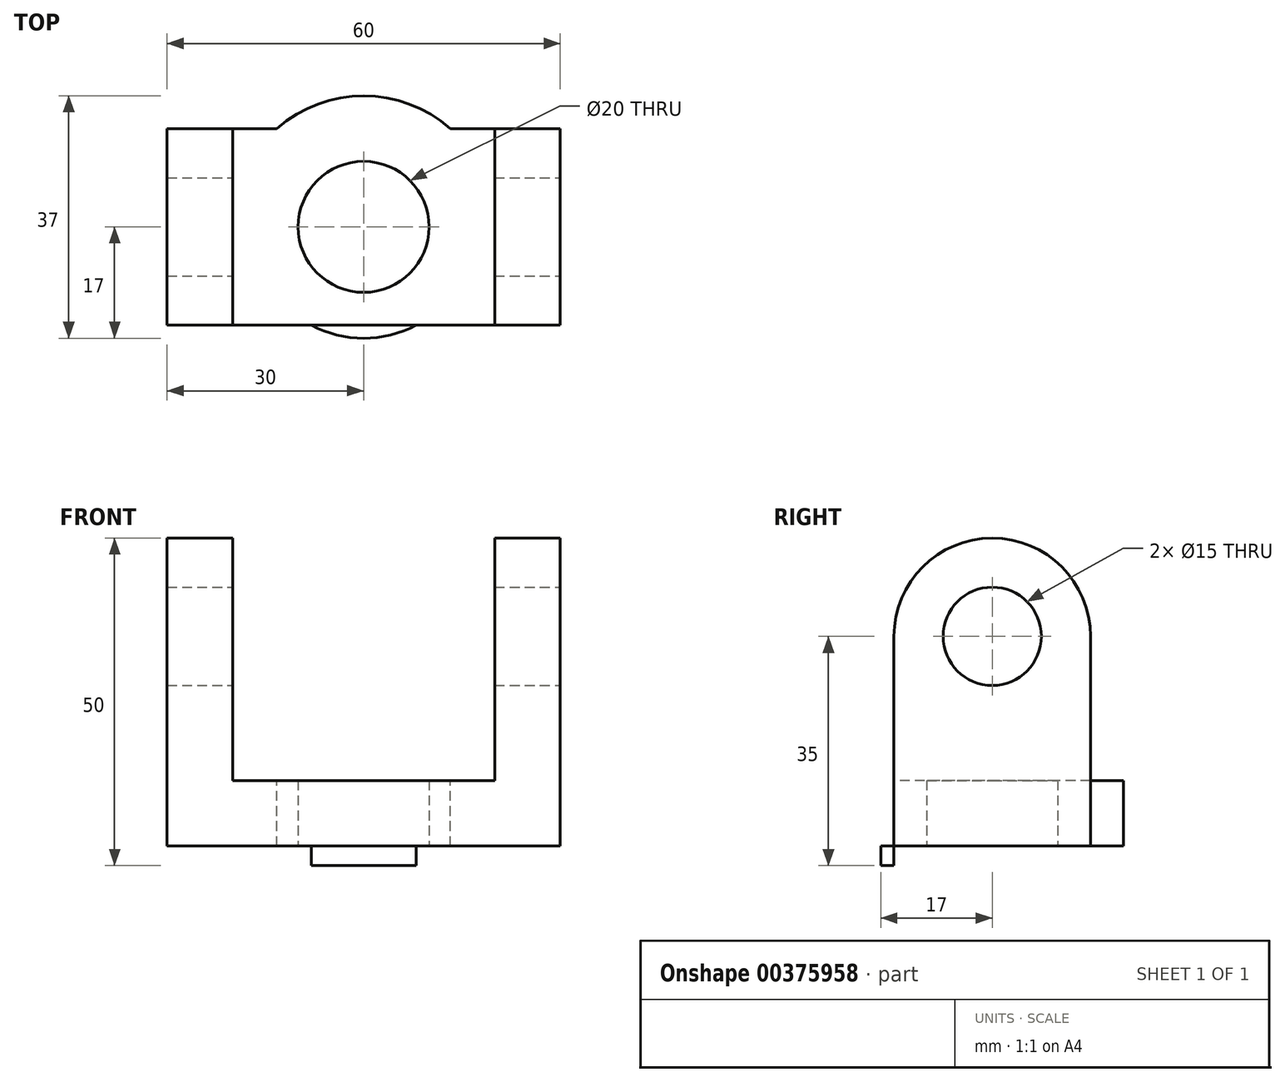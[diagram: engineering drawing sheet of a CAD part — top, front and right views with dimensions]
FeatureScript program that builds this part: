
annotation { "Feature Type Name" : "Feature", "Feature Type Description" : "" }
export const myFeature = defineFeature(function(context is Context, id is Id, definition is map)
    precondition{}
    {
        {
            var Q0;
            Q0=qCreatedBy(makeId("Top.planeOp"),FACE);
            var sketch = newSketch(context, id + "F0", { "sketchPlane" : qUnion([Q0])});
            skLineSegment(sketch, "E0.bottom", {"start": v(0, 0) * mm, "end": v(60, 0) * mm});
            skLineSegment(sketch, "E0.top", {"start": v(0, 30) * mm, "end": v(60, 30) * mm});
            skLineSegment(sketch, "E0.left", {"start": v(0, 0) * mm, "end": v(0, 30) * mm});
            skLineSegment(sketch, "E0.right", {"start": v(60, 0) * mm, "end": v(60, 30) * mm});
            skCircle(sketch, "E1", {"center": v(30, 15) * mm, "radius": 10 * mm});
            skPoint(sketch, "E1.centerSnap0", {"position": v(30, 30) * mm});
            skPoint(sketch, "E1.centerSnap1", {"position": v(0, 15) * mm});
            skSolve(sketch);
        }
        {
            var Q0;
            Q0 = qSketchRegion(id + "F0", true);
            extrude(context, id + "F1", {"entities" : qUnion([Q0]), "depth" : 10 * mm});
        }
        {
            var Q0;
            Q0=makeQuery(id+"F1.opExtrude","CAP_FACE",FACE,{"disambiguationData":[OSD([sQuery(id+"F0.wireOp",EDGE,"E0.bottom"),sQuery(id+"F0.wireOp",EDGE,"E0.top"),sQuery(id+"F0.wireOp",EDGE,"E0.left"),sQuery(id+"F0.wireOp",EDGE,"E0.right"),sQuery(id+"F0.wireOp",EDGE,"E1")])],"isStart":false});
            var sketch = newSketch(context, id + "F2", { "sketchPlane" : qUnion([Q0])});
            skArc(sketch, "E2", {"start": v(50, 15) * mm, "mid": v(30, 35) * mm, "end": v(10, 15) * mm});
            skPoint(sketch, "E3", {"position": v(0, 15) * mm});
            skPoint(sketch, "E4", {"position": v(60, 15) * mm});
            skLineSegment(sketch, "E5", {"start": v(0, 15) * mm, "end": v(60, 15) * mm, "construction": true});
            skArc(sketch, "E6.MirrorCS", {"start": v(50, 15) * mm, "mid": v(30, -5) * mm, "end": v(10, 15) * mm});
            skSolve(sketch);
        }
        {
            var Q0;
            {var subQ0=sQuery(id+"F2.wireOp",EDGE,"E2");var subQ1=makeQuery(id+"F1.opExtrude","CAP_EDGE",EDGE,{"disambiguationData":[OSD([sQuery(id+"F0.wireOp",EDGE,"E0.top")])],"isStart":false});var subQ2=makeQuery(id+"F2.imprint","INTERSECT",VERTEX,{"disambiguationData":[OD(0.0)],"derivedFrom":[subQ1,subQ0]});Q0=makeQuery(id+"F2.imprint","IMPRINT",FACE,{"disambiguationData":[TD([[makeQuery(id+"F2.imprint","IMPRINT",EDGE,{"disambiguationData":[TD([[subQ2,-1.0]])],"derivedFrom":subQ0}),1.0]])]});}
            var Q1;
            {var subQ0=sQuery(id+"F2.wireOp",EDGE,"E6.MirrorCS");var subQ1=makeQuery(id+"F1.opExtrude","CAP_EDGE",EDGE,{"disambiguationData":[OSD([sQuery(id+"F0.wireOp",EDGE,"E0.bottom")])],"isStart":false});var subQ2=makeQuery(id+"F2.imprint","INTERSECT",VERTEX,{"disambiguationData":[OD(0.0)],"derivedFrom":[subQ1,subQ0]});Q1=makeQuery(id+"F2.imprint","IMPRINT",FACE,{"disambiguationData":[TD([[makeQuery(id+"F2.imprint","IMPRINT",EDGE,{"disambiguationData":[TD([[subQ2,-1.0]])],"derivedFrom":subQ0}),-1.0]])]});}
            extrude(context, id + "F3", {"entities" : qUnion([Q0, Q1]), "operationType" : NewBodyOperationType.ADD, "oppositeDirection" : true, "depth" : 10 * mm});
        }
        {
            var Q0;
            {var subQ0=sQuery(id+"F0.wireOp",EDGE,"E0.bottom");var subQ1=sQuery(id+"F0.wireOp",EDGE,"E0.top");Q0=makeQuery(id+"F3.boolean.opBoolean","MERGE",FACE,{"derivedFrom":[makeQuery(id+"F1.opExtrude","CAP_FACE",FACE,{"disambiguationData":[OSD([subQ0,subQ1,sQuery(id+"F0.wireOp",EDGE,"E0.left"),sQuery(id+"F0.wireOp",EDGE,"E0.right"),sQuery(id+"F0.wireOp",EDGE,"E1")])],"isStart":true}),makeQuery(id+"F3.opExtrude","CAP_FACE",FACE,{"disambiguationData":[OSD([subQ1,sQuery(id+"F2.wireOp",EDGE,"E2")])],"isStart":false}),makeQuery(id+"F3.opExtrude","CAP_FACE",FACE,{"disambiguationData":[OSD([subQ0,sQuery(id+"F2.wireOp",EDGE,"E6.MirrorCS")])],"isStart":false})]});}
            var sketch = newSketch(context, id + "F4", { "sketchPlane" : qUnion([Q0])});
            skCircle(sketch, "E7", {"center": v(30, -15) * mm, "radius": 17 * mm});
            skSolve(sketch);
        }
        {
            var Q0;
            Q0=makeQuery(id+"F4.imprint","IMPRINT",FACE,{"disambiguationData":[TD([[makeQuery(id+"F4.imprint","IMPRINT",EDGE,{"derivedFrom":sQuery(id+"F4.wireOp",EDGE,"E7")}),1.0]])]});
            extrude(context, id + "F5", {"entities" : qUnion([Q0]), "operationType" : NewBodyOperationType.ADD, "depth" : 3 * mm});
        }
        {
            var Q0;
            Q0=makeQuery(id+"F1.opExtrude","SWEPT_FACE",FACE,{"disambiguationData":[OSD([sQuery(id+"F0.wireOp",EDGE,"E0.right")])]});
            var sketch = newSketch(context, id + "F6", { "sketchPlane" : qUnion([Q0])});
            skPoint(sketch, "E8.0", {"position": v(0, 10) * mm});
            skPoint(sketch, "E9.0", {"position": v(30, 10) * mm});
            skLineSegment(sketch, "E10.bottom", {"start": v(0, 10) * mm, "end": v(30, 10) * mm});
            skLineSegment(sketch, "E10.top", {"start": v(0, 32) * mm, "end": v(7.5, 32) * mm});
            skLineSegment(sketch, "E10.left", {"start": v(0, 10) * mm, "end": v(0, 32) * mm});
            skLineSegment(sketch, "E10.right", {"start": v(30, 10) * mm, "end": v(30, 32) * mm});
            skArc(sketch, "E11", {"start": v(30, 32) * mm, "mid": v(15, 47) * mm, "end": v(0, 32) * mm});
            skCircle(sketch, "E12", {"center": v(15, 32) * mm, "radius": 7.5 * mm});
            skLineSegment(sketch, "E13.trimOffspring", {"start": v(22.5, 32) * mm, "end": v(30, 32) * mm});
            skSolve(sketch);
        }
        {
            var Q0;
            Q0 = qSketchRegion(id + "F6", true);
            var Q1;
            Q1=makeQuery(id+"F1.opExtrude","SWEPT_FACE",FACE,{"disambiguationData":[OSD([sQuery(id+"F0.wireOp",EDGE,"E0.left")])]});
            extrude(context, id + "F7", {"entities" : qUnion([Q0]), "operationType" : NewBodyOperationType.ADD, "endBound" : BoundingType.UP_TO_SURFACE, "oppositeDirection" : true, "endBoundEntityFace" : qUnion([Q1]), "depth" : 25 * mm});
        }
        {
            var Q0;
            Q0=qCreatedBy(makeId("Front.planeOp"),FACE);
            var sketch = newSketch(context, id + "F8", { "sketchPlane" : qUnion([Q0])});
            skPoint(sketch, "E14.0", {"position": v(30, 10) * mm});
            skLineSegment(sketch, "E15.bottom", {"start": v(10, 51) * mm, "end": v(50, 51) * mm});
            skLineSegment(sketch, "E15.top", {"start": v(10, 10) * mm, "end": v(50, 10) * mm});
            skLineSegment(sketch, "E15.left", {"start": v(10, 51) * mm, "end": v(10, 10) * mm});
            skLineSegment(sketch, "E15.right", {"start": v(50, 51) * mm, "end": v(50, 10) * mm});
            skSolve(sketch);
        }
        {
            var Q0;
            Q0 = qSketchRegion(id + "F8", true);
            extrude(context, id + "F9", {"entities" : qUnion([Q0]), "operationType" : NewBodyOperationType.REMOVE, "endBound" : BoundingType.THROUGH_ALL, "oppositeDirection" : true, "depth" : 25 * mm});
        }
    });
